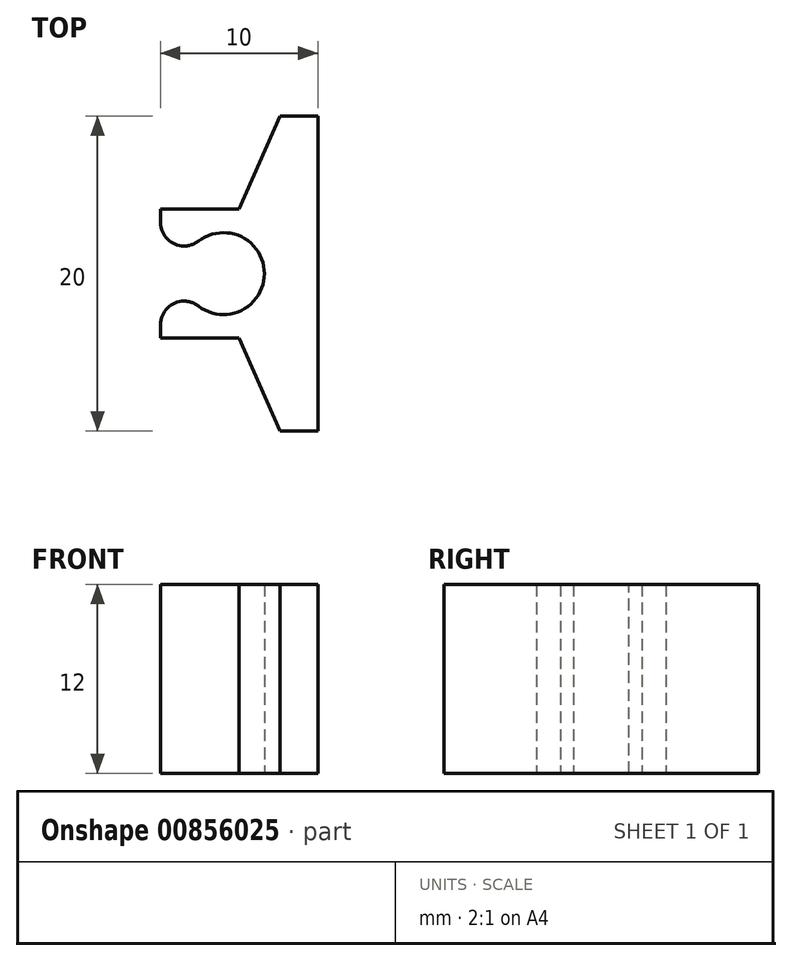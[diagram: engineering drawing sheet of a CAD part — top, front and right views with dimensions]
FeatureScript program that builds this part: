
annotation { "Feature Type Name" : "Feature", "Feature Type Description" : "" }
export const myFeature = defineFeature(function(context is Context, id is Id, definition is map)
    precondition{}
    {
        {
            var Q0;
            Q0=qCreatedBy(makeId("Top.planeOp"),FACE);
            var sketch = newSketch(context, id + "F0", { "sketchPlane" : qUnion([Q0])});
            skLineSegment(sketch, "E0.bottom", {"start": v(-32.55, -27.6) * mm, "end": v(-22.55, -27.6) * mm});
            skLineSegment(sketch, "E0.top", {"start": v(-32.55, -35.8) * mm, "end": v(-22.55, -35.8) * mm});
            skLineSegment(sketch, "E0.left", {"start": v(-32.55, -27.6) * mm, "end": v(-32.55, -35.8) * mm});
            skLineSegment(sketch, "E0.right", {"start": v(-22.55, -27.6) * mm, "end": v(-22.55, -35.8) * mm});
            skLineSegment(sketch, "E1", {"start": v(-32.55, -31.7) * mm, "end": v(-28.55, -31.7) * mm, "construction": true});
            skLineSegment(sketch, "E2", {"start": v(-32.55, -31.7) * mm, "end": v(-32.55, -29.95) * mm, "construction": true});
            skLineSegment(sketch, "E3", {"start": v(-32.55, -31.7) * mm, "end": v(-32.55, -33.45) * mm, "construction": true});
            skCircle(sketch, "E4", {"center": v(-28.55, -31.7) * mm, "radius": 2.6 * mm});
            skLineSegment(sketch, "E5.bottom", {"start": v(-32.55, -29.95) * mm, "end": v(-30.47, -29.95) * mm});
            skLineSegment(sketch, "E5.top", {"start": v(-32.55, -33.45) * mm, "end": v(-30.47, -33.45) * mm});
            skLineSegment(sketch, "E5.left", {"start": v(-32.55, -29.95) * mm, "end": v(-32.55, -33.45) * mm});
            skLineSegment(sketch, "E5.right", {"start": v(-30.47, -29.95) * mm, "end": v(-30.47, -33.45) * mm});
            skLineSegment(sketch, "E6", {"start": v(-22.55, -31.7) * mm, "end": v(-24.95, -31.7) * mm, "construction": true});
            skLineSegment(sketch, "E7.bottom", {"start": v(-22.55, -21.7) * mm, "end": v(-24.95, -21.7) * mm});
            skLineSegment(sketch, "E7.top", {"start": v(-22.55, -41.7) * mm, "end": v(-24.95, -41.7) * mm});
            skLineSegment(sketch, "E7.left", {"start": v(-22.55, -21.7) * mm, "end": v(-22.55, -41.7) * mm});
            skLineSegment(sketch, "E7.right", {"start": v(-24.95, -21.7) * mm, "end": v(-24.95, -41.7) * mm});
            skPoint(sketch, "E7.middle", {"position": v(-23.75, -31.7) * mm});
            skLineSegment(sketch, "E8", {"start": v(-24.95, -21.7) * mm, "end": v(-27.55, -27.6) * mm});
            skLineSegment(sketch, "E9", {"start": v(-24.95, -41.7) * mm, "end": v(-27.55, -35.8) * mm});
            skSolve(sketch);
        }
        {
            var Q0;
            {var subQ12=sQuery(id+"F0.wireOp",EDGE,"E5.bottom");Q0=makeQuery(id+"F0.imprint","IMPRINT",FACE,{"disambiguationData":[TD([[makeQuery(id+"F0.imprint","IMPRINT",EDGE,{"derivedFrom":subQ12}),1.0]])]});}
            var Q1;
            {var subQ0=sQuery(id+"F0.wireOp",EDGE,"E8");Q1=makeQuery(id+"F0.imprint","IMPRINT",FACE,{"disambiguationData":[TD([[makeQuery(id+"F0.imprint","IMPRINT",EDGE,{"derivedFrom":subQ0}),1.0]])]});}
            var Q2;
            {var subQ5=sQuery(id+"F0.wireOp",EDGE,"E7.bottom");Q2=makeQuery(id+"F0.imprint","IMPRINT",FACE,{"disambiguationData":[TD([[makeQuery(id+"F0.imprint","IMPRINT",EDGE,{"derivedFrom":subQ5}),1.0]])]});}
            var Q3;
            {var subQ0=sQuery(id+"F0.wireOp",EDGE,"E7.left");var subQ1=sQuery(id+"F0.wireOp",EDGE,"E0.bottom");var subQ2=makeQuery(id+"F0.imprint","INTERSECT",VERTEX,{"derivedFrom":[subQ1,subQ0]});Q3=makeQuery(id+"F0.imprint","IMPRINT",FACE,{"disambiguationData":[TD([[makeQuery(id+"F0.imprint","IMPRINT",EDGE,{"disambiguationData":[TD([[subQ2,1.0]])],"derivedFrom":subQ1}),-1.0]])]});}
            var Q4;
            {var subQ5=sQuery(id+"F0.wireOp",EDGE,"E7.top");Q4=makeQuery(id+"F0.imprint","IMPRINT",FACE,{"disambiguationData":[TD([[makeQuery(id+"F0.imprint","IMPRINT",EDGE,{"derivedFrom":subQ5}),-1.0]])]});}
            var Q5;
            {var subQ0=sQuery(id+"F0.wireOp",EDGE,"E9");Q5=makeQuery(id+"F0.imprint","IMPRINT",FACE,{"disambiguationData":[TD([[makeQuery(id+"F0.imprint","IMPRINT",EDGE,{"derivedFrom":subQ0}),-1.0]])]});}
            extrude(context, id + "F1", {"entities" : qUnion([Q0, Q1, Q2, Q3, Q4, Q5]), "depth" : 12 * mm, "offsetDistance" : 25 * mm});
        }
        {
            var Q0;
            Q0=makeQuery(id+"F1.opExtrude","SWEPT_EDGE",EDGE,{"disambiguationData":[OSD([sQuery(id+"F0.wireOp",EDGE,"E0.left"),sQuery(id+"F0.wireOp",EDGE,"E5.top"),sQuery(id+"F0.wireOp",EDGE,"E5.left")])]});
            var Q1;
            Q1=makeQuery(id+"F1.opExtrude","SWEPT_EDGE",EDGE,{"disambiguationData":[OSD([sQuery(id+"F0.wireOp",EDGE,"E0.left"),sQuery(id+"F0.wireOp",EDGE,"E5.bottom"),sQuery(id+"F0.wireOp",EDGE,"E5.left")])]});
            fillet(context, id + "F2", {"entities" : qUnion([Q0, Q1]), "radius" : 1.5 * mm, "tangentPropagation" : true, "allowEdgeOverflow" : false});
        }
        {
            var Q0;
            Q0=makeQuery(id+"F1.opExtrude","SWEPT_EDGE",EDGE,{"disambiguationData":[OSD([sQuery(id+"F0.wireOp",EDGE,"E4"),sQuery(id+"F0.wireOp",EDGE,"E5.bottom"),sQuery(id+"F0.wireOp",EDGE,"E5.right")])]});
            var Q1;
            Q1=makeQuery(id+"F1.opExtrude","SWEPT_EDGE",EDGE,{"disambiguationData":[OSD([sQuery(id+"F0.wireOp",EDGE,"E4"),sQuery(id+"F0.wireOp",EDGE,"E5.top"),sQuery(id+"F0.wireOp",EDGE,"E5.right")])]});
            fillet(context, id + "F3", {"entities" : qUnion([Q0, Q1]), "radius" : 1.5 * mm, "tangentPropagation" : true, "allowEdgeOverflow" : false});
        }
    });
